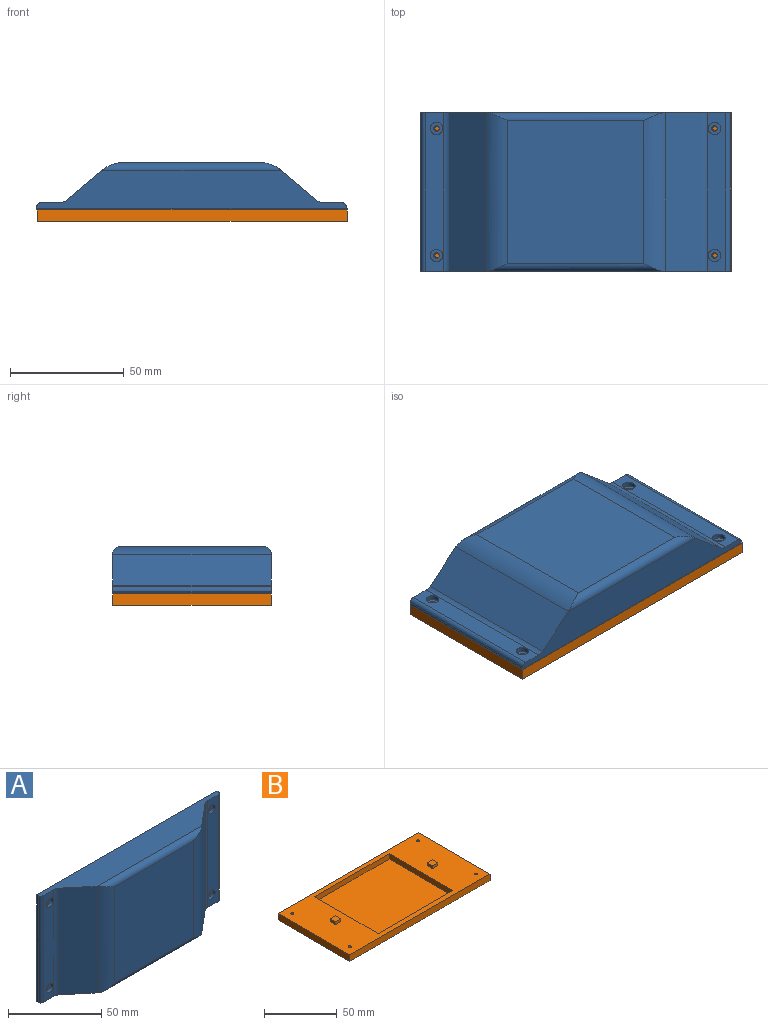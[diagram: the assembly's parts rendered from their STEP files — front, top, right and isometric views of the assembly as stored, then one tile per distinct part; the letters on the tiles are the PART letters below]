
ASSEMBLY  parts=2 mates=1
PART A: 45 faces, bbox 136.5x20.7x70 mm
  f0: plane 136.45x70mm, normal (0,1,0), area 4848.3mm2, adj f4,f5,f12,f13,f18,f19,f20,f21
  f1: plane 63x60mm, normal (0,-1,0), area 3780mm2, adj f2,f3,f16,f17
  f2: cylinder r=15mm len=70mm, axis (0,0,-1), area 704.8mm2, adj f1,f4,f5,f7,f16,f17
  f3: cylinder r=15mm len=70mm, axis (0,0,-1), area 704.8mm2, adj f1,f4,f5,f8,f16,f17
  f4: plane 136.46x17.21mm, normal (0,0,1), area 1774.3mm2, adj f0,f2,f3,f6,f7,f8,f9,f10
  f5: plane 136.45x17.19mm, normal (0,0,-1), area 1773.2mm2, adj f0,f2,f3,f6,f7,f8,f9,f10
  f6: cylinder r=5mm len=70mm, axis (0,0,-1), area 183.3mm2, adj f4,f5,f7,f15
  f7: plane 70x16.06mm, normal (-0.64,-0.77,0), area 1467.2mm2, adj f2,f4,f5,f6
  f8: plane 70x16.06mm, normal (0.64,-0.77,0), area 1467.2mm2, adj f3,f4,f5,f9
  f9: cylinder r=5mm len=70mm, axis (0,0,-1), area 183.3mm2, adj f4,f5,f8,f10
  f10: plane 70x8.03mm, normal (0,-1,0), area 514.4mm2, adj f4,f5,f9,f11,f37,f39
  f11: cylinder r=2mm len=70mm, axis (0,0,-1), area 219.9mm2, adj f4,f5,f10,f12
  f12: plane 70x1.03mm, normal (1,0,0), area 72.4mm2, adj f0,f4,f5,f11
  f13: plane 70x1.03mm, normal (-1,0,0), area 72.4mm2, adj f0,f4,f5,f14
  f14: cylinder r=2mm len=70mm, axis (0,0,-1), area 219.9mm2, adj f4,f5,f13,f15
  f15: plane 70x8.03mm, normal (0,-1,0), area 514.4mm2, adj f4,f5,f6,f14,f33,f35
  f16: cylinder r=3.5mm len=79.23mm, axis (1,0,0), area 386.3mm2, adj f1,f2,f3,f4
  f17: cylinder r=3.5mm len=79.26mm, axis (1,0,0), area 387.4mm2, adj f1,f2,f3,f5
  f18: plane 63.4x16.69mm, normal (1,0,0), area 1057.9mm2, adj f0,f19,f21,f22
  f19: plane 72.8x16.69mm, normal (0,0,1), area 1214.8mm2, adj f0,f18,f20,f22
  f20: plane 63.4x16.69mm, normal (-1,0,0), area 1057.9mm2, adj f0,f19,f21,f22
  f21: plane 72.8x16.69mm, normal (0,0,-1), area 1214.8mm2, adj f0,f18,f20,f22
  f22: plane 72.8x63.4mm, normal (0,1,0), area 4615.5mm2, adj f18,f19,f20,f21
  f23: plane 5.9x3mm, normal (0,0,1), area 17.7mm2, adj f0,f24,f26,f27
  f24: plane 5.9x3mm, normal (1,0,0), area 17.7mm2, adj f0,f23,f25,f27
  f25: plane 5.9x3mm, normal (0,0,-1), area 17.7mm2, adj f0,f24,f26,f27
  f26: plane 5.9x3mm, normal (-1,0,0), area 17.7mm2, adj f0,f23,f25,f27
  f27: plane 5.9x5.9mm, normal (0,1,0), area 34.8mm2, adj f23,f24,f25,f26
  f28: plane 5.9x3mm, normal (0,0,-1), area 17.7mm2, adj f0,f29,f31,f32
  f29: plane 5.9x3mm, normal (-1,0,0), area 17.7mm2, adj f0,f28,f30,f32
  f30: plane 5.9x3mm, normal (0,0,1), area 17.7mm2, adj f0,f29,f31,f32
  f31: plane 5.9x3mm, normal (1,0,0), area 17.7mm2, adj f0,f28,f30,f32
  f32: plane 5.9x5.9mm, normal (0,1,0), area 34.8mm2, adj f28,f29,f30,f31
  f33: cylinder r=2.75mm len=5.5mm, axis (0,-1,0), area 35.2mm2, adj f15,f34
  f34: plane 5.5x5.5mm, normal (0,-1,0), area 19.2mm2, adj f33,f44
  f35: cylinder r=2.75mm len=5.5mm, axis (0,-1,0), area 35.2mm2, adj f15,f36
  f36: plane 5.5x5.5mm, normal (0,-1,0), area 19.2mm2, adj f35,f43
  f37: cylinder r=2.75mm len=5.5mm, axis (0,-1,0), area 35.2mm2, adj f10,f38
  f38: plane 5.5x5.5mm, normal (0,-1,0), area 19.2mm2, adj f37,f42
  f39: cylinder r=2.75mm len=5.5mm, axis (0,-1,0), area 35.2mm2, adj f10,f40
  f40: plane 5.5x5.5mm, normal (0,-1,0), area 19.2mm2, adj f39,f41
  f41: cylinder r=1.2mm len=2.4mm, axis (0,1,0), area 7.5mm2, adj f0,f40
  f42: cylinder r=1.2mm len=2.4mm, axis (0,1,0), area 7.5mm2, adj f0,f38
  f43: cylinder r=1.2mm len=2.4mm, axis (0,1,0), area 7.5mm2, adj f0,f36
  f44: cylinder r=1.2mm len=2.4mm, axis (0,1,0), area 7.5mm2, adj f0,f34
PART B: 29 faces, bbox 136.5x70x8 mm
  f0: plane 136.5x70mm, normal (0,0,1), area 4964.8mm2, adj f1,f2,f3,f4,f6,f7,f8,f9
  f1: plane 136.5x5.5mm, normal (0,-1,0), area 750.8mm2, adj f0,f2,f4,f5
  f2: plane 70x5.5mm, normal (1,0,0), area 385mm2, adj f0,f1,f3,f5
  f3: plane 136.5x5.5mm, normal (0,1,0), area 750.8mm2, adj f0,f2,f4,f5
  f4: plane 70x5.5mm, normal (-1,0,0), area 385mm2, adj f0,f1,f3,f5
  f5: plane 136.5x70mm, normal (0,0,-1), area 9555mm2, adj f1,f2,f3,f4
  f6: plane 72.8x4.5mm, normal (0,1,0), area 327.6mm2, adj f0,f7,f9,f10
  f7: plane 62.1x4.5mm, normal (-1,0,0), area 279.4mm2, adj f0,f6,f8,f10
  f8: plane 72.8x4.5mm, normal (0,-1,0), area 327.6mm2, adj f0,f7,f9,f10
  f9: plane 62.1x4.5mm, normal (1,0,0), area 279.4mm2, adj f0,f6,f8,f10
  f10: plane 72.8x62.1mm, normal (0,0,1), area 4520.9mm2, adj f6,f7,f8,f9
  f11: plane 5.2x2.5mm, normal (0,1,0), area 13mm2, adj f0,f12,f14,f15
  f12: plane 5.2x2.5mm, normal (1,0,0), area 13mm2, adj f0,f11,f13,f15
  f13: plane 5.2x2.5mm, normal (0,-1,0), area 13mm2, adj f0,f12,f14,f15
  f14: plane 5.2x2.5mm, normal (-1,0,0), area 13mm2, adj f0,f11,f13,f15
  f15: plane 5.2x5.2mm, normal (0,0,1), area 27mm2, adj f11,f12,f13,f14
  f16: plane 5.2x2.5mm, normal (-1,0,0), area 13mm2, adj f0,f17,f19,f20
  f17: plane 5.2x2.5mm, normal (0,1,0), area 13mm2, adj f0,f16,f18,f20
  f18: plane 5.2x2.5mm, normal (1,0,0), area 13mm2, adj f0,f17,f19,f20
  f19: plane 5.2x2.5mm, normal (0,-1,0), area 13mm2, adj f0,f16,f18,f20
  f20: plane 5.2x5.2mm, normal (0,0,1), area 27mm2, adj f16,f17,f18,f19
  f21: cylinder r=1.1mm len=4mm, axis (0,0,1), area 27.6mm2, adj f0,f22
  f22: plane 2.2x2.2mm, normal (0,0,1), area 3.8mm2, adj f21
  f23: cylinder r=1.1mm len=4mm, axis (0,0,1), area 27.6mm2, adj f0,f24
  f24: plane 2.2x2.2mm, normal (0,0,1), area 3.8mm2, adj f23
  f25: cylinder r=1.1mm len=4mm, axis (0,0,1), area 27.6mm2, adj f0,f26
  f26: plane 2.2x2.2mm, normal (0,0,1), area 3.8mm2, adj f25
  f27: cylinder r=1.1mm len=4mm, axis (0,0,1), area 27.6mm2, adj f0,f28
  f28: plane 2.2x2.2mm, normal (0,0,1), area 3.8mm2, adj f27
PLACE A rot(axis=(-1,0,0),90deg) t=(65.82,-35,65.79)mm
PLACE B t=(-2.38,0,78.32)mm
MATE fastened B.f12 <-> A.f26  axis (1,0,0) through (-47.03,0,85.07)mm
